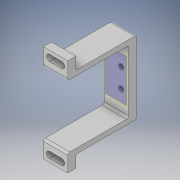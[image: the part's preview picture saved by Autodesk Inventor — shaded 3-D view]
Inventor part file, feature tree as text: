
AUTODESK INVENTOR PART (.ipt)
format: ipt  version: 2019 (Build 230136000, 136)  size: 503,808 bytes
history: native  units: mm
features: sketch x4, extrude x4, fillet x3, other x3, plane x2, mirror x1
ambient origin geometry x8: Origin, YZ Plane, XZ Plane, XY Plane, X Axis, Y Axis, Z Axis, Center Point
bodies: Solid1 (feature_tree)
feature tree (17):
  sketch  "Sketch1"  dims[d0=12.0mm d1=31.0mm]
  plane  "Work Plane1"
  plane  "Work Plane2"
  extrude  "Extrusion1"  Depth=31.0mm
  sketch  "Sketch5"  dims[d2=4.95mm d3=2.5mm]
  extrude  "Extrusion5"  Depth=2.5mm
  extrude  "Extrusion6"  Depth=2.5mm
  extrude  "Extrusion7"  Depth=1.0mm
  fillet  "Fillet3"  Radius=2.5mm
  mirror  "Mirror2"
  fillet  "Fillet4"  Radius=4.0mm
  fillet  "Fillet5"  Radius=20.75mm
  sketch  "Sketch6"  dims[d4=4.81mm d5=2.5mm]
  sketch  "Sketch7"  dims[d6=2.5mm d7=4.69mm d8=2.5mm d9=4.0mm d10=0.0mm d33=20.75mm d34=12.0mm d35=41.5mm d36=3.0mm d37=3.1mm d38=12.0mm d39=31.0mm d40=12.0mm d41=2.5mm d42=30.0mm d43=4.0mm d44=0.0mm d45=0.0mm d46=12.0mm d47=4.0mm d48=6.0mm d49=19.6mm d50=6.0mm d51=0.0mm d52=6.0mm d53=0.0mm d54=0.5mm d55=0.5mm d56=1.0mm d57=1.0mm d58=0.5mm d59=1.0mm]
  other  "<userpath>\Desktop\PWR\SEM7\INZYNIER\maszyna\Maszyna1.iam"
  other  "Maszyna1.iam"
  other  "endstop_maszyna:1"
